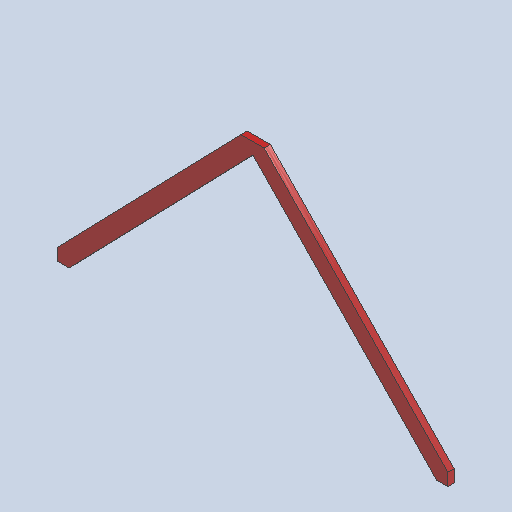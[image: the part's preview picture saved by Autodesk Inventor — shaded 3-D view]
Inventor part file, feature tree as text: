
AUTODESK INVENTOR PART (.ipt)
format: ipt  version: 2025 (Build 290162000, 162)  size: 101,376 bytes
history: native  units: in
note: dims shown in document units (in); Inventor stores cm internally (conversion verified against a paired STEP export)
features: other x4, sketch x1
ambient origin geometry x8: Origin, YZ Plane, XZ Plane, XY Plane, X Axis, Y Axis, Z Axis, Center Point
bodies: Solid1 (feature_tree)
feature tree (5):
  other  "48x2x4-2.ipt"
  other  "Solid1::48x2x4-2.ipt"
  other  "TaggingFeature1"
  sketch  "Sketch1"  dims[d0=0.3937in]
  other  "Finish1"
